# Revit family: QF_ELECTROLUXPROFESSIONAL_589272_MCADEAHDAO
name_source: partatom
category: Specialty Equipment
revit_build: Autodesk Revit 2018 (Build: 20190510_1515(x64)
units: mm (PartAtom-declared; Revit-internal decimal feet)

## family parameters
Always vertical = Yes
Cut with Voids When Loaded = No
Part Type = Normal
Room Calculation Point = No
Round Connector Dimension = Use Diameter
Shared = No
Work Plane-Based = No

## types (1)
- QF_ELECTROLUXPROFESSIONAL_589272_MCADEAHDAO
    Apparent Power = 10200 VA
    Conn Conduit = Yes
    Description = EL.MULTIBRAISER,2/1GN,1SIDE,800X900X700H
    Direct Waste Size = 0"
    FL Amps = 15 A
    HP = 13.7 HP
    Manufacturer = ELECTROLUX
    Max Overcurrent Protection = 0 A
    Min Ckt Ampacity = 0 A
    Model = 589272
    Phase = 3
    URL = www.electrolux.com/professional
    URL Cutsheet = www.electrolux.com/professional
    Volts = 400 V
    Watts = 10200 W
    Weight in Pounds = 330.69

## geometry (parser evidence)
native form markers: Blend x2, Sweep x9
no freeform markers — native parametric forms only
